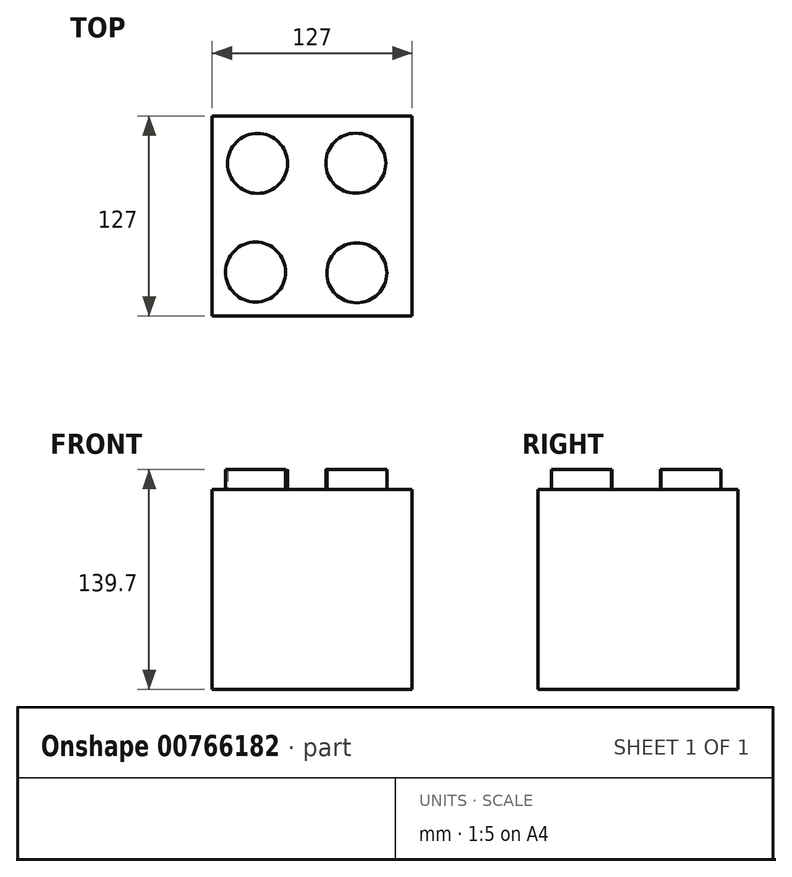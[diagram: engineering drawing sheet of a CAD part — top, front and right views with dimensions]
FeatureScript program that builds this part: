
annotation { "Feature Type Name" : "Feature", "Feature Type Description" : "" }
export const myFeature = defineFeature(function(context is Context, id is Id, definition is map)
    precondition{}
    {
        {
            var Q0;
            Q0=qCreatedBy(makeId("Front.planeOp"),FACE);
            var sketch = newSketch(context, id + "F0", { "sketchPlane" : qUnion([Q0])});
            skLineSegment(sketch, "E0.bottom", {"start": v(-63.5, 56.75) * mm, "end": v(63.5, 56.75) * mm});
            skLineSegment(sketch, "E0.top", {"start": v(-63.5, -70.25) * mm, "end": v(63.5, -70.25) * mm});
            skLineSegment(sketch, "E0.left", {"start": v(-63.5, 56.75) * mm, "end": v(-63.5, -70.25) * mm});
            skLineSegment(sketch, "E0.right", {"start": v(63.5, 56.75) * mm, "end": v(63.5, -70.25) * mm});
            skSolve(sketch);
        }
        {
            var Q0;
            Q0=makeQuery(id+"F0.imprint","IMPRINT",FACE,{"disambiguationData":[TD([[makeQuery(id+"F0.imprint","IMPRINT",EDGE,{"derivedFrom":sQuery(id+"F0.wireOp",EDGE,"E0.bottom")}),-1.0]])]});
            extrude(context, id + "F1", {"entities" : qUnion([Q0]), "depth" : 127 * mm, "offsetDistance" : 25.4 * mm});
        }
        {
            var Q0;
            Q0=makeQuery(id+"F1.opExtrude","SWEPT_FACE",FACE,{"disambiguationData":[OSD([sQuery(id+"F0.wireOp",EDGE,"E0.bottom")])]});
            var sketch = newSketch(context, id + "F2", { "sketchPlane" : qUnion([Q0])});
            skCircle(sketch, "E1", {"center": v(-34.68, -30.08) * mm, "radius": 19.05 * mm});
            skCircle(sketch, "E2", {"center": v(27.73, -29.93) * mm, "radius": 19.05 * mm});
            skCircle(sketch, "E3", {"center": v(-35.94, -99.13) * mm, "radius": 19.05 * mm});
            skCircle(sketch, "E4", {"center": v(28.36, -99.6) * mm, "radius": 19.05 * mm});
            skSolve(sketch);
        }
        {
            var Q0;
            Q0=makeQuery(id+"F2.imprint","IMPRINT",FACE,{"disambiguationData":[TD([[makeQuery(id+"F2.imprint","IMPRINT",EDGE,{"derivedFrom":sQuery(id+"F2.wireOp",EDGE,"E1")}),1.0]])]});
            var Q1;
            Q1=makeQuery(id+"F2.imprint","IMPRINT",FACE,{"disambiguationData":[TD([[makeQuery(id+"F2.imprint","IMPRINT",EDGE,{"derivedFrom":sQuery(id+"F2.wireOp",EDGE,"E2")}),1.0]])]});
            var Q2;
            Q2=makeQuery(id+"F2.imprint","IMPRINT",FACE,{"disambiguationData":[TD([[makeQuery(id+"F2.imprint","IMPRINT",EDGE,{"derivedFrom":sQuery(id+"F2.wireOp",EDGE,"E3")}),1.0]])]});
            var Q3;
            Q3=makeQuery(id+"F2.imprint","IMPRINT",FACE,{"disambiguationData":[TD([[makeQuery(id+"F2.imprint","IMPRINT",EDGE,{"derivedFrom":sQuery(id+"F2.wireOp",EDGE,"E4")}),1.0]])]});
            extrude(context, id + "F3", {"entities" : qUnion([Q0, Q1, Q2, Q3]), "operationType" : NewBodyOperationType.ADD, "depth" : 12.7 * mm, "offsetDistance" : 25.4 * mm});
        }
    });
